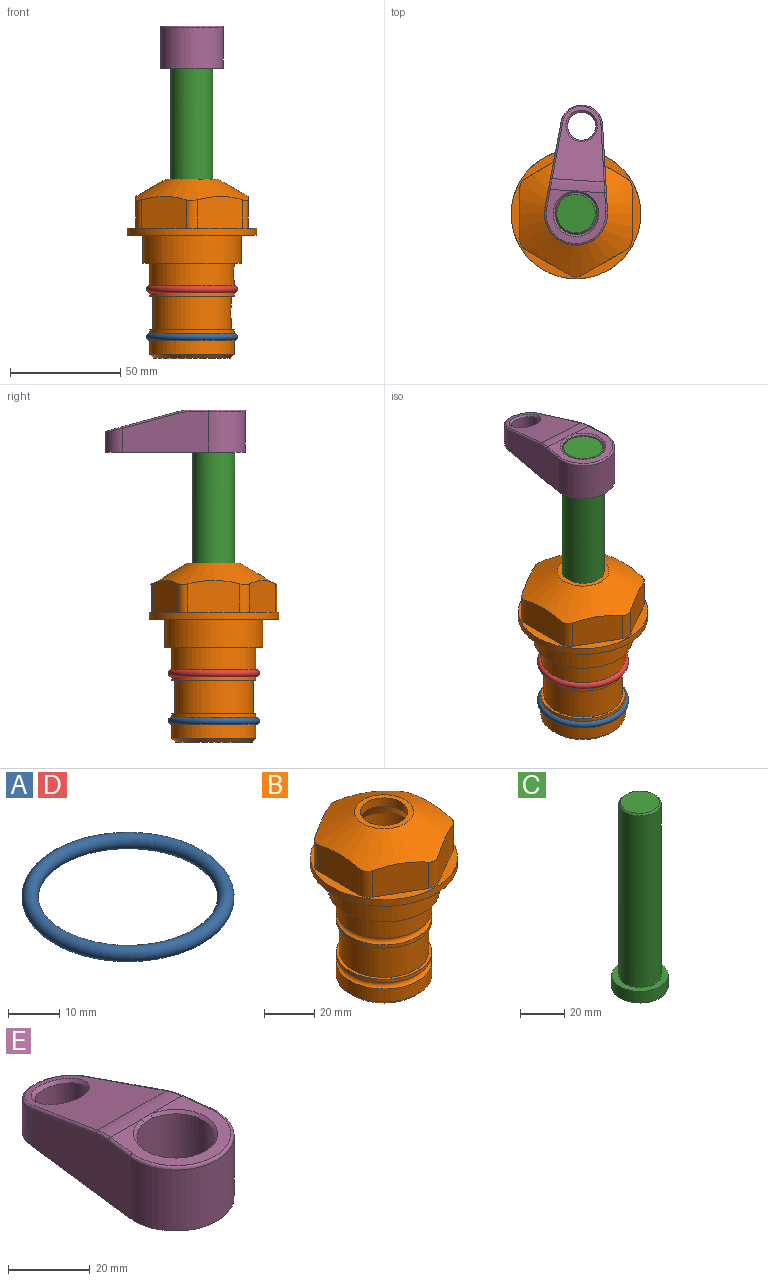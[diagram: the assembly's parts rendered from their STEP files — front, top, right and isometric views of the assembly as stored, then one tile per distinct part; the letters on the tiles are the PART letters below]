
ASSEMBLY  parts=5 mates=4
PART A: 1 faces, bbox 44.7x44.7x3.2 mm
  f0: torus R=19.05mm, axis (0,0,1), area 1193.9mm2
PART B: 36 faces, bbox 58.7x58.7x81 mm
  f0: cylinder r=17.78mm len=35.56mm, axis (0,0,1), area 1670.8mm2, adj f23,f24,f31
  f1: cylinder r=19.05mm len=38.1mm, axis (0,0,1), area 1191.9mm2, adj f26,f27,f30
  f2: plane 58.66x58.66mm, normal (0,0,-1), area 1150.6mm2, adj f3,f28
  f3: cylinder r=29.33mm len=58.66mm, axis (0,0,-1), area 585.1mm2, adj f2,f4
  f4: plane 58.66x58.66mm, normal (0,0,1), area 475.9mm2, adj f3,f5,f6,f7,f8,f9,f10,f11
  f5: plane 20.32x14.34mm, normal (-0.5,0.87,0), area 324.4mm2, adj f4,f15,f16,f17
  f6: plane 20.32x14.34mm, normal (0.5,0.87,0), area 324.4mm2, adj f4,f14,f15,f17
  f7: plane 23.48x14.34mm, normal (1,0,0), area 324.4mm2, adj f4,f13,f14,f17
  f8: plane 20.32x14.34mm, normal (0.5,-0.87,0), area 324.4mm2, adj f4,f12,f13,f17
  f9: plane 20.32x14.34mm, normal (-0.5,-0.87,0), area 324.4mm2, adj f4,f11,f12,f17
  f10: plane 23.48x14.34mm, normal (-1,0,0), area 324.4mm2, adj f4,f11,f16,f17
  f11: cylinder r=5.08mm len=12.85mm, axis (0,0,-1), area 67.2mm2, adj f4,f9,f10,f17
  f12: cylinder r=5.08mm len=12.85mm, axis (0,0,-1), area 67.2mm2, adj f4,f8,f9,f17
  f13: cylinder r=5.08mm len=12.85mm, axis (0,0,-1), area 67.2mm2, adj f4,f7,f8,f17
  f14: cylinder r=5.08mm len=12.85mm, axis (0,0,-1), area 67.2mm2, adj f4,f6,f7,f17
  f15: cylinder r=5.08mm len=12.85mm, axis (0,0,-1), area 67.2mm2, adj f4,f5,f6,f17
  f16: cylinder r=5.08mm len=12.85mm, axis (0,0,-1), area 67.2mm2, adj f4,f5,f10,f17
  f17: cone r=11.73mm half-angle=60deg, axis (0,0,-1), area 2071.8mm2, adj f5,f6,f7,f8,f9,f10,f11,f12
  f18: plane 23.46x23.46mm, normal (0,0,1), area 147.4mm2, adj f17,f35
  f19: plane 34.93x34.93mm, normal (0,0,-1), area 958mm2, adj f29
  f20: cylinder r=19.05mm len=38.1mm, axis (0,0,1), area 760.1mm2, adj f21,f29
  f21: torus R=19.05mm, axis (0,0,1), area 565.3mm2, adj f20,f22
  f22: cylinder r=19.05mm len=38.1mm, axis (0,0,1), area 190mm2, adj f21,f23
  f23: plane 38.1x38.1mm, normal (0,0,1), area 146.9mm2, adj f0,f22
  f24: plane 38.1x38.1mm, normal (0,0,-1), area 146.9mm2, adj f0,f25
  f25: cylinder r=19.05mm len=38.1mm, axis (0,0,1), area 190mm2, adj f24,f26
  f26: torus R=19.05mm, axis (0,0,1), area 565.3mm2, adj f1,f25
  f27: plane 44.45x44.45mm, normal (0,0,-1), area 411.7mm2, adj f1,f28
  f28: cylinder r=22.23mm len=44.45mm, axis (0,0,1), area 1773.5mm2, adj f2,f27
  f29: cone r=19.05mm half-angle=45deg, axis (0,0,1), area 257.5mm2, adj f19,f20
  f30: cylinder r=3.17mm len=6.75mm, axis (-1,0,0), area 128mm2, adj f1,f33
  f31: cylinder r=3.17mm len=6.35mm, axis (-1,0,0), area 102.5mm2, adj f0,f33
  f32: plane 25.4x25.4mm, normal (0,0,1), area 506.7mm2, adj f33
  f33: cylinder r=12.7mm len=66.42mm, axis (0,0,-1), area 5236.2mm2, adj f30,f31,f32,f34
  f34: cone r=9.53mm half-angle=30deg, axis (0,0,-1), area 443.4mm2, adj f33,f35
  f35: cylinder r=9.53mm len=19.05mm, axis (0,0,-1), area 240.9mm2, adj f18,f34
PART C: 6 faces, bbox 25.4x25.4x101.6 mm
  f0: plane 17.46x17.46mm, normal (0,0,1), area 239.5mm2, adj f5
  f1: plane 25.4x25.4mm, normal (0,0,-1), area 506.7mm2, adj f2
  f2: cylinder r=12.7mm len=25.4mm, axis (0,0,1), area 506.7mm2, adj f1,f3
  f3: plane 25.4x25.4mm, normal (0,0,1), area 221.7mm2, adj f2,f4
  f4: cylinder r=9.53mm len=94.46mm, axis (0,0,1), area 5653mm2, adj f3,f5
  f5: cone r=8.73mm half-angle=45deg, axis (0,0,-1), area 64.4mm2, adj f0,f4
PART D: same geometry as A
PART E: 31 faces, bbox 31.7x65.5x19.8 mm
  f0: plane 39.12x18.26mm, normal (0.99,0.12,0), area 612.2mm2, adj f1,f4,f7,f11,f13,f15
  f1: cylinder r=9.53mm len=18.91mm, axis (0,0,-1), area 296.1mm2, adj f0,f2,f7,f17
  f2: plane 39.12x18.26mm, normal (-0.99,0.12,0), area 612.2mm2, adj f1,f4,f7,f12,f14,f16
  f3: cylinder r=6.35mm len=12.7mm, axis (0,0,-1), area 362.4mm2, adj f7,f18
  f4: cylinder r=14.29mm len=28.58mm, axis (0,0,-1), area 882.2mm2, adj f0,f2,f7,f10
  f5: cylinder r=9.53mm len=19.05mm, axis (0,0,-1), area 1092.6mm2, adj f7,f19,f20
  f6: plane 26.99x23.69mm, normal (0,0,1), area 216.2mm2, adj f9,f10,f11,f12,f19
  f7: plane 63.5x28.58mm, normal (0,0,-1), area 661.8mm2, adj f0,f1,f2,f3,f4,f5,f22,f23
  f8: plane 33.52x23.6mm, normal (0,0.26,0.97), area 486mm2, adj f9,f15,f16,f17,f18
  f9: cylinder r=19.05mm len=24.72mm, axis (1,0,0), area 120.4mm2, adj f6,f8,f13,f14,f20
  f10: torus R=13.49mm, axis (0,0,1), area 59mm2, adj f4,f6,f11,f12
  f11: cylinder r=0.79mm len=8.67mm, axis (0.12,-0.99,0), area 10.8mm2, adj f0,f6,f10,f13
  f12: cylinder r=0.79mm len=8.67mm, axis (0.12,0.99,0), area 10.8mm2, adj f2,f6,f10,f14
  f13: bspline ~4.95x1.42mm, area 6.1mm2, adj f0,f9,f11,f15
  f14: bspline ~4.95x1.42mm, area 6.1mm2, adj f2,f9,f12,f16
  f15: cylinder r=0.79mm len=25.95mm, axis (0.12,-0.96,0.26), area 32.9mm2, adj f0,f8,f13,f17
  f16: cylinder r=0.79mm len=25.95mm, axis (0.12,0.96,-0.26), area 32.9mm2, adj f2,f8,f14,f17
  f17: bspline ~18.91x8.38mm, area 30mm2, adj f1,f8,f15,f16
  f18: bspline ~14.29x14.29mm, area 48.3mm2, adj f3,f8
  f19: cone r=9.53mm half-angle=45deg, axis (0,0,1), area 66.5mm2, adj f5,f6,f20
  f20: bspline ~3.22x0.96mm, area 3.5mm2, adj f5,f9,f19
  f21: plane 2.75x2.72mm, normal (0,0,-1), area 2.9mm2, adj f23,f25,f28
  f22: plane 23.05x15.88mm, normal (-0.99,-0.12,0), area 323.6mm2, adj f7,f25,f26,f27,f28,f29
  f23: plane 23.05x15.88mm, normal (0.99,-0.12,0), area 323.6mm2, adj f7,f21,f25,f27,f28,f30
  f24: cylinder r=9.53mm len=10.69mm, axis (0,0,-1), area 114.7mm2, adj f7,f27,f29,f30
  f25: cylinder r=12.7mm len=20.59mm, axis (0,0,-1), area 381.1mm2, adj f7,f21,f22,f23,f26,f28
  f26: plane 2.75x2.72mm, normal (0,0,-1), area 2.9mm2, adj f22,f25,f28
  f27: plane 19.72x18.37mm, normal (0,-0.26,-0.97), area 291.8mm2, adj f22,f23,f24,f28,f29,f30
  f28: cylinder r=15.88mm len=19.92mm, axis (1,0,0), area 54.8mm2, adj f21,f22,f23,f25,f26,f27
  f29: cylinder r=1.59mm len=11mm, axis (0,0,-1), area 34.7mm2, adj f7,f22,f24,f27
  f30: cylinder r=1.59mm len=11mm, axis (0,0,-1), area 34.7mm2, adj f7,f23,f24,f27
PLACE A t=(0,0,-21.59)mm
PLACE B at identity fixed
PLACE C rot(axis=(0,0,-1),3.7deg) t=(0,0,30.41)mm
PLACE D at identity
PLACE E rot(axis=(0,0,-1),3.7deg) t=(0,0,31.21)mm
MATE fastened A.f0 <-> B.f0  axis (0,0,1) through (0,0,-46.1)mm
MATE cylindrical C.f2 <-> B.f0  axis (0,0,-1) through (0,0,-7.69)mm
MATE fastened E.f4 <-> C.f2  axis (0,0,-1) through (0,0,93.91)mm
MATE fastened D.f0 <-> B.f0  axis (0,0,1) through (0,0,-24.51)mm
